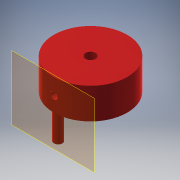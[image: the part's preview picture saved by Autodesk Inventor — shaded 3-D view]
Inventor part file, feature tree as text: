
AUTODESK INVENTOR PART (.ipt)
format: ipt  version: 2016 (Build 200138000, 138)  size: 129,536 bytes
history: native  units: mm
features: reference x6, sketch x4, plane x4, extrude x3, thicken_offset x2, hole x1
ambient origin geometry x8: Origin, YZ Plane, XZ Plane, XY Plane, X Axis, Y Axis, Z Axis, Center Point
bodies: Solid1 (feature_tree)
feature tree (20):
  sketch  "Sketch1"  dims[d0=10.0mm d1=0.0mm d2=10.0mm d3=0.0mm]
  plane  "Work Plane1"
  extrude  "Extrusion1"  Depth=10.0mm TaperAngle=0.0deg
  sketch  "Sketch2"  dims[d4=15.0mm d5=0.0mm]
  plane  "Work Plane2"
  extrude  "Extrusion2"  TaperAngle=0.0deg  [1 undecoded]
  extrude  "Extrusion3"  Depth=2.0mm
  plane  "Work Plane4"
  hole  "Hole1"  [1 undecoded]
  thicken_offset  "Thicken1"
  thicken_offset  "Thicken2"
  reference  "Reference1"
  reference  "Reference2"
  reference  "Reference3"
  reference  "Reference4"
  reference  "Reference5"
  reference  "Reference6"
  sketch  "Sketch3"  dims[d6=0.6mm d7=0.6mm]
  plane  "Work Plane3"
  sketch  "Sketch4"  dims[d8=4.0mm d9=6.0mm d10=4.0mm d11=2.0mm d12=90.0deg d13=8.0mm d14=20.594885mm d15=0.4mm d16=0.4mm]
note: 2 required parameter values undecoded (feature->parameter linkage not recoverable at this tier; creation-order binding heuristic only, values carry confidence <= 0.55)
